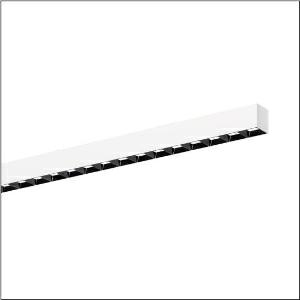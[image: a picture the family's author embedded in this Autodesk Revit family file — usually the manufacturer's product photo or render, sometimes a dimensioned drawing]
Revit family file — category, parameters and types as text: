
# Revit family: silica_r__21_51mx21da44wb_a3a2
name_source: partatom
category: Lighting Fixtures
units: mm (PartAtom-declared; Revit-internal decimal feet)

## family parameters
Cut with Voids When Loaded = No
Host = Face
Light Source = No
Part Type = Normal
Room Calculation Point = No
Round Connector Dimension = Use Diameter
Shared = No

## types (1)
- --- (1 x LED, 4320 lm, 25.6 W, 4000K)
    Apparent Load = 26 VA
    CIE Flux Codes = 87 99 100 100 100
    Color Rendering = 80
    Color Temperature = 4000K
    Default Elevation = 1800 mm
    Description = Silica® 21, office luminaire, primary light control with darklight reflector, of PMMA, black, CAT 2 (L<= 3000cd/m²), light emission: direct distribution, primary light characteristic: symmetric, installation type: surface-mounted, LED, rated luminous flux: 4.320lm, luminous efficacy: 169lm/W, light colour: 840, colour temperature: 4000K, with terminal, 3+2-pole, max. 2.5mm², mains connection: 220..240V, AC, 50/60Hz, rated input power: 25.6W, luminaire housing, of aluminium, traffic white (RAL 9016), length: 1.204mm, width: 53mm, height: 53mm, protection rating (complete): IP20, insulation class (complete): insulation class I (protective earthing), certification: CE, permissible operating ambient temperature: 0..+35°C, standard: EN 50419, packaging unit: 1 piece
    Height = 0 mm  [stored 0 ft]
    Lamp = 1 x LED
    Lamp Light Flux = 4320 lm
    Lamp Power = 25.6 W
    Lamp count = 1
    Length = 1204 mm
    Luminous efficacy = 169 lm/W
    Manufacturer = Siteco
    ModVariant = No
    Model = 51MX21DA44WB
    Mounting Place = Ceiling
    Mounting Type = Recessed
    Number of Poles = 1
    OnlyDefault = Yes
    Power Factor = 1
    Product Name = Silica® 21
    Product group = office luminaire | ceiling recessed
    ProductGroupID = 401
    Protection Class = Protection class I
    Protection Degree = IP 20
    RLX_Detail_Level = 1
    RLX_Emergency_Light_Flux = 0 lm
    RLX_Emergency_Type = 0
    RLX_Emergency_Type_DB = No
    RlxData = <blob elided: 42037 chars, md5=91c6de6a>
    Socket = socket
    Standby Power = 0 W
    System Light Flux = 4320 lm
    System Power = 26 W
    Type Comments = factory setting: luminous flux: 100 % | dim-lin: 254 | 367 mA
    Type Image = l_1313592.jpg
    URL = http://relux.com
    VarID = @adj_073147
    Voltage = 0 V
    Weight = 0.00 kg
    Width = 53 mm

note: [stored X ft] marks values corroborated as IEEE doubles in the binary element streams (Revit-internal decimal feet)

## geometry (parser evidence)
native form markers: Blend x4, Sweep x9
no freeform markers — native parametric forms only
